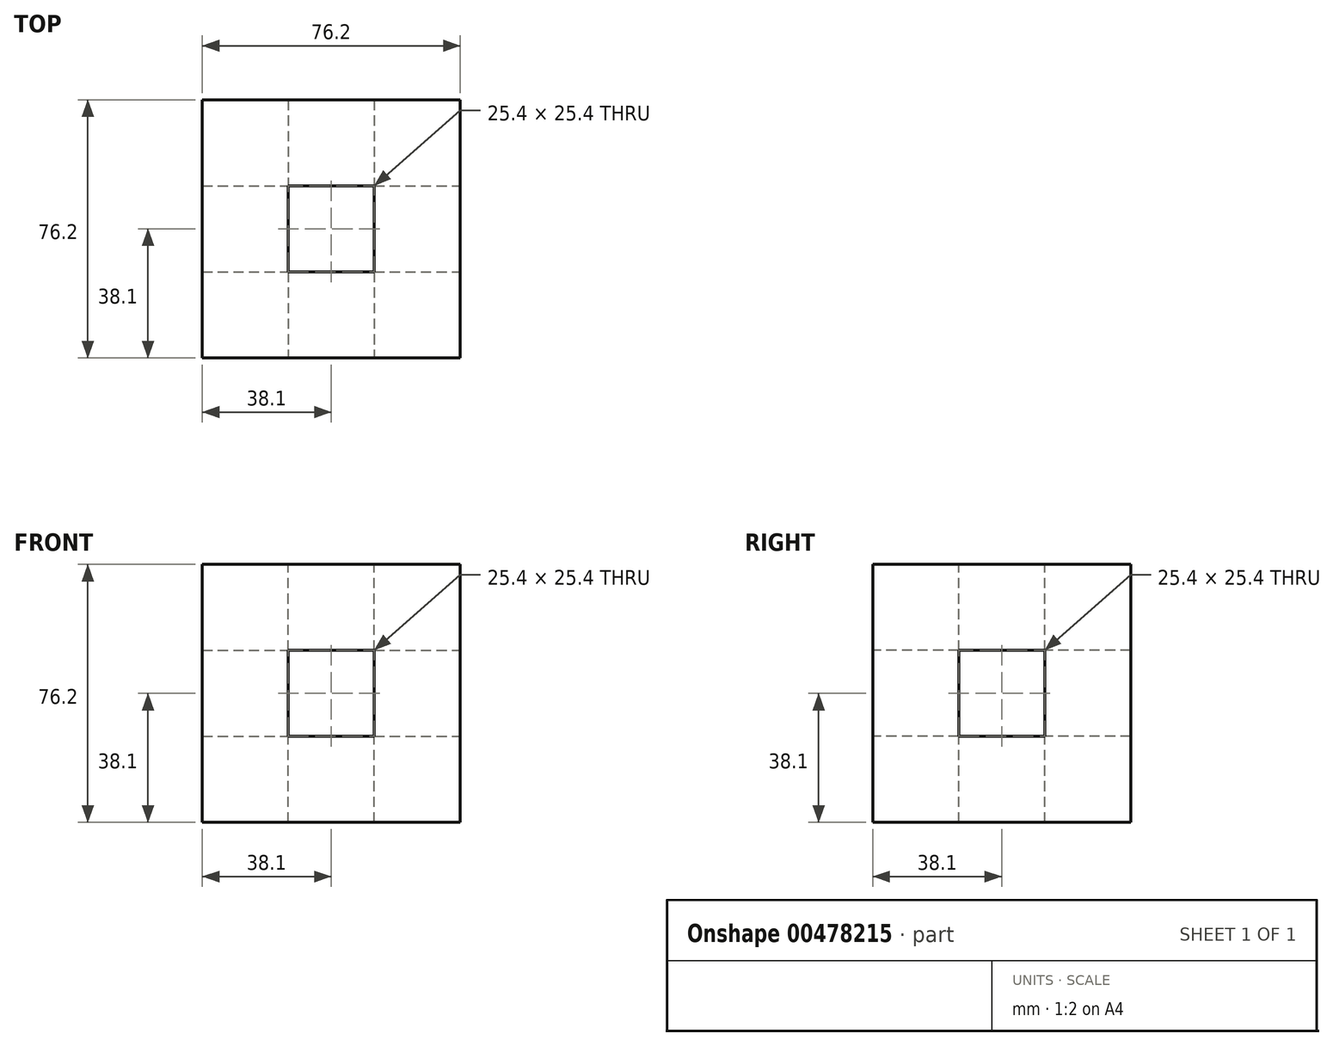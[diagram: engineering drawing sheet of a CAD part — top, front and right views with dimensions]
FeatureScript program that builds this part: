
annotation { "Feature Type Name" : "Feature", "Feature Type Description" : "" }
export const myFeature = defineFeature(function(context is Context, id is Id, definition is map)
    precondition{}
    {
        {
            var Q0;
            Q0=qCreatedBy(makeId("Front.planeOp"),FACE);
            var sketch = newSketch(context, id + "F0", { "sketchPlane" : qUnion([Q0])});
            skLineSegment(sketch, "E0", {"start": v(0, 0) * mm, "end": v(0, 76.2) * mm});
            skLineSegment(sketch, "E1", {"start": v(0, 76.2) * mm, "end": v(76.2, 76.2) * mm});
            skLineSegment(sketch, "E2", {"start": v(76.2, 76.2) * mm, "end": v(76.2, 0) * mm});
            skLineSegment(sketch, "E3", {"start": v(76.2, 0) * mm, "end": v(0, 0) * mm});
            skSolve(sketch);
        }
        {
            var Q0;
            Q0=makeQuery(id+"F0.imprint","IMPRINT",FACE,{"disambiguationData":[TD([[makeQuery(id+"F0.imprint","IMPRINT",EDGE,{"derivedFrom":sQuery(id+"F0.wireOp",EDGE,"E0")}),-1.0]])]});
            extrude(context, id + "F1", {"entities" : qUnion([Q0]), "depth" : 76.2 * mm});
        }
        {
            var Q0;
            Q0=makeQuery(id+"F1.opExtrude","CAP_FACE",FACE,{"disambiguationData":[OSD([sQuery(id+"F0.wireOp",EDGE,"E0"),sQuery(id+"F0.wireOp",EDGE,"E1"),sQuery(id+"F0.wireOp",EDGE,"E2"),sQuery(id+"F0.wireOp",EDGE,"E3")])],"isStart":false});
            var sketch = newSketch(context, id + "F2", { "sketchPlane" : qUnion([Q0])});
            skLineSegment(sketch, "E4.bottom", {"start": v(25.4, 25.4) * mm, "end": v(50.8, 25.4) * mm});
            skLineSegment(sketch, "E4.top", {"start": v(25.4, 50.8) * mm, "end": v(50.8, 50.8) * mm});
            skLineSegment(sketch, "E4.left", {"start": v(25.4, 25.4) * mm, "end": v(25.4, 50.8) * mm});
            skLineSegment(sketch, "E4.right", {"start": v(50.8, 25.4) * mm, "end": v(50.8, 50.8) * mm});
            skSolve(sketch);
        }
        {
            var Q0;
            Q0=makeQuery(id+"F2.imprint","IMPRINT",FACE,{"disambiguationData":[TD([[makeQuery(id+"F2.imprint","IMPRINT",EDGE,{"derivedFrom":sQuery(id+"F2.wireOp",EDGE,"E4.bottom")}),1.0]])]});
            extrude(context, id + "F3", {"entities" : qUnion([Q0]), "operationType" : NewBodyOperationType.REMOVE, "oppositeDirection" : true, "depth" : 76.2 * mm});
        }
        {
            var Q0;
            Q0=makeQuery(id+"F1.opExtrude","SWEPT_FACE",FACE,{"disambiguationData":[OSD([sQuery(id+"F0.wireOp",EDGE,"E1")])]});
            var sketch = newSketch(context, id + "F4", { "sketchPlane" : qUnion([Q0])});
            skLineSegment(sketch, "E5.bottom", {"start": v(25.4, -25.4) * mm, "end": v(50.8, -25.4) * mm});
            skLineSegment(sketch, "E5.top", {"start": v(25.4, -50.8) * mm, "end": v(50.8, -50.8) * mm});
            skLineSegment(sketch, "E5.left", {"start": v(25.4, -25.4) * mm, "end": v(25.4, -50.8) * mm});
            skLineSegment(sketch, "E5.right", {"start": v(50.8, -25.4) * mm, "end": v(50.8, -50.8) * mm});
            skSolve(sketch);
        }
        {
            var Q0;
            Q0=makeQuery(id+"F4.imprint","IMPRINT",FACE,{"disambiguationData":[TD([[makeQuery(id+"F4.imprint","IMPRINT",EDGE,{"derivedFrom":sQuery(id+"F4.wireOp",EDGE,"E5.bottom")}),-1.0]])]});
            extrude(context, id + "F5", {"entities" : qUnion([Q0]), "operationType" : NewBodyOperationType.REMOVE, "oppositeDirection" : true, "depth" : 76.2 * mm});
        }
        {
            var Q0;
            Q0=makeQuery(id+"F1.opExtrude","SWEPT_FACE",FACE,{"disambiguationData":[OSD([sQuery(id+"F0.wireOp",EDGE,"E2")])]});
            var sketch = newSketch(context, id + "F6", { "sketchPlane" : qUnion([Q0])});
            skLineSegment(sketch, "E6.bottom", {"start": v(-50.8, 50.8) * mm, "end": v(-25.4, 50.8) * mm});
            skLineSegment(sketch, "E6.top", {"start": v(-50.8, 25.4) * mm, "end": v(-25.4, 25.4) * mm});
            skLineSegment(sketch, "E6.left", {"start": v(-50.8, 50.8) * mm, "end": v(-50.8, 25.4) * mm});
            skLineSegment(sketch, "E6.right", {"start": v(-25.4, 50.8) * mm, "end": v(-25.4, 25.4) * mm});
            skSolve(sketch);
        }
        {
            var Q0;
            Q0=makeQuery(id+"F6.imprint","IMPRINT",FACE,{"disambiguationData":[TD([[makeQuery(id+"F6.imprint","IMPRINT",EDGE,{"derivedFrom":sQuery(id+"F6.wireOp",EDGE,"E6.bottom")}),-1.0]])]});
            extrude(context, id + "F7", {"entities" : qUnion([Q0]), "operationType" : NewBodyOperationType.REMOVE, "oppositeDirection" : true, "depth" : 76.2 * mm});
        }
    });
